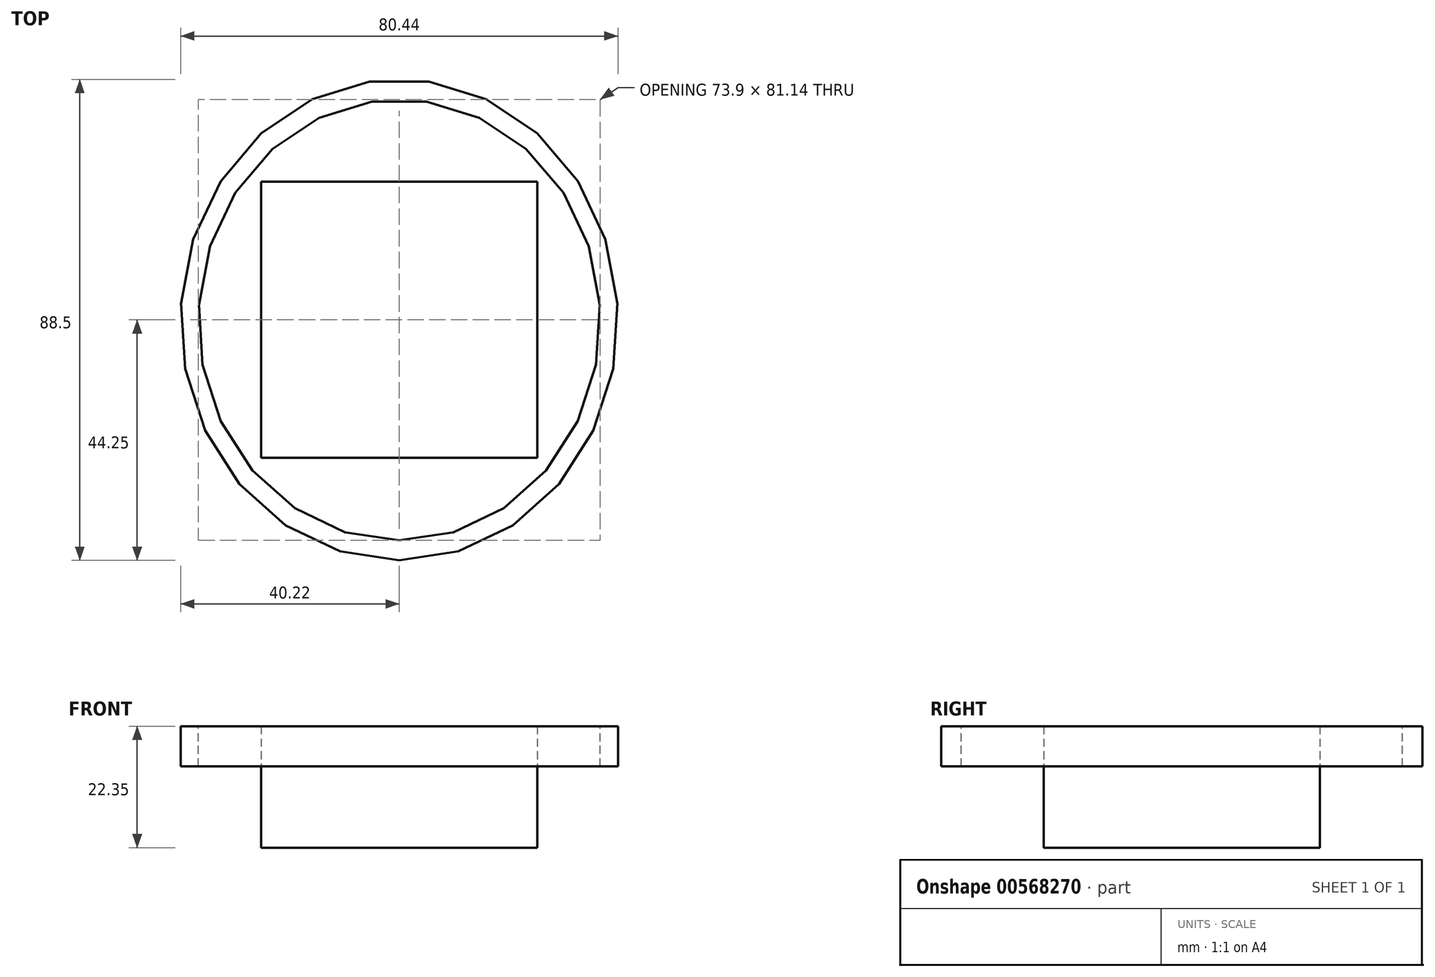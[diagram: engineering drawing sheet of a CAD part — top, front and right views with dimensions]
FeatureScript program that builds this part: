
annotation { "Feature Type Name" : "Feature", "Feature Type Description" : "" }
export const myFeature = defineFeature(function(context is Context, id is Id, definition is map)
    precondition{}
    {
        {
            var Q0;
            Q0=qCreatedBy(makeId("Top.planeOp"),FACE);
            var sketch = newSketch(context, id + "F0", { "sketchPlane" : qUnion([Q0])});
            skLineSegment(sketch, "E0.bottom", {"start": v(25.4, -25.4) * mm, "end": v(-25.4, -25.4) * mm});
            skLineSegment(sketch, "E0.top", {"start": v(25.4, 25.4) * mm, "end": v(-25.4, 25.4) * mm});
            skLineSegment(sketch, "E0.left", {"start": v(25.4, -25.4) * mm, "end": v(25.4, 25.4) * mm});
            skLineSegment(sketch, "E0.right", {"start": v(-25.4, -25.4) * mm, "end": v(-25.4, 25.4) * mm});
            skPoint(sketch, "E0.middle", {"position": v(0, 0) * mm});
            skSolve(sketch);
        }
        {
            var Q0;
            Q0 = qSketchRegion(id + "F0", true);
            extrude(context, id + "F1", {"entities" : qUnion([Q0]), "depth" : 22.35 * mm, "offsetDistance" : 25 * mm});
        }
        {
            var Q0;
            Q0=makeQuery(id+"F1.opExtrude","CAP_FACE",FACE,{"disambiguationData":[OSD([sQuery(id+"F0.wireOp",EDGE,"E0.bottom"),sQuery(id+"F0.wireOp",EDGE,"E0.top"),sQuery(id+"F0.wireOp",EDGE,"E0.left"),sQuery(id+"F0.wireOp",EDGE,"E0.right")])],"isStart":false});
            var sketch = newSketch(context, id + "F2", { "sketchPlane" : qUnion([Q0])});
            skEllipse(sketch, "E1", {"center": v(0, 0) * mm, "majorRadius": 40.57 * mm, "minorRadius": 36.95 * mm, "majorAxis": v(0, -1)});
            skEllipse(sketch, "E2", {"center": v(0, 0) * mm, "majorRadius": 44.25 * mm, "minorRadius": 40.22 * mm, "majorAxis": v(0, -1)});
            skSolve(sketch);
        }
        {
            var Q0;
            Q0 = qSketchRegion(id + "F2", true);
            extrude(context, id + "F3", {"entities" : qUnion([Q0]), "oppositeDirection" : true, "depth" : 7.4 * mm, "offsetDistance" : 25 * mm});
        }
    });
